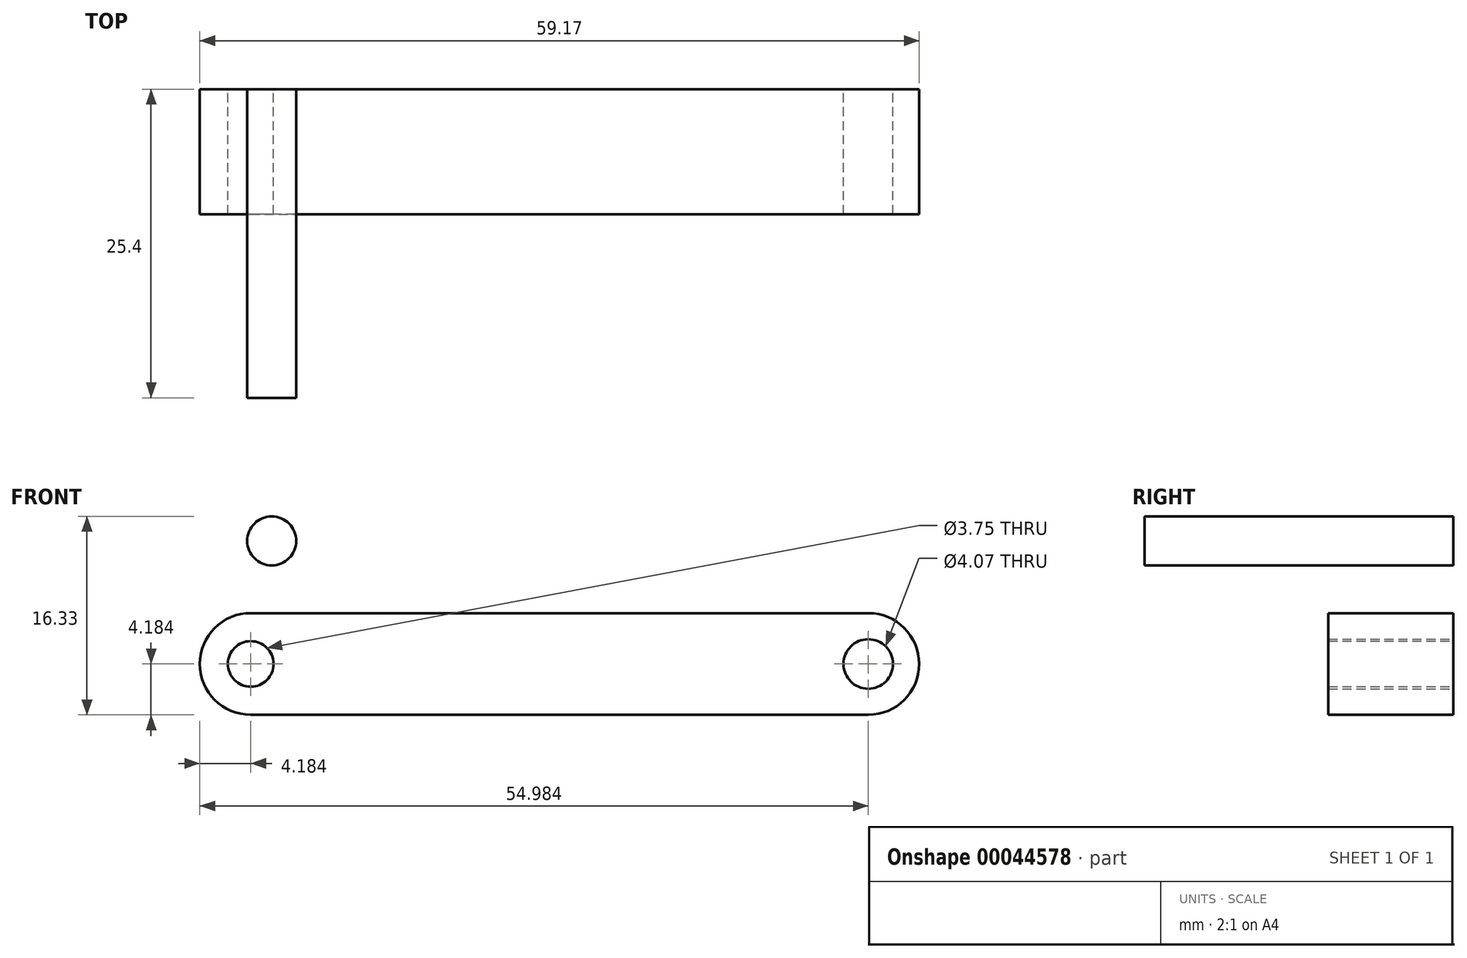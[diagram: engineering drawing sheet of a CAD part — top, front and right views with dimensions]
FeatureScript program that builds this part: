
annotation { "Feature Type Name" : "Feature", "Feature Type Description" : "" }
export const myFeature = defineFeature(function(context is Context, id is Id, definition is map)
    precondition{}
    {
        {
            var Q0;
            Q0=qCreatedBy(makeId("Front.planeOp"),FACE);
            var sketch = newSketch(context, id + "F0", { "sketchPlane" : qUnion([Q0])});
            skLineSegment(sketch, "E0", {"start": v(-62.77, 44.12) * mm, "end": v(-11.97, 44.12) * mm});
            skArc(sketch, "E1", {"start": v(-11.97, 35.75) * mm, "mid": v(-7.78, 39.93) * mm, "end": v(-11.97, 44.12) * mm});
            skLineSegment(sketch, "E2", {"start": v(-11.97, 35.75) * mm, "end": v(-62.77, 35.75) * mm});
            skArc(sketch, "E3", {"start": v(-62.77, 44.12) * mm, "mid": v(-66.95, 39.93) * mm, "end": v(-62.77, 35.75) * mm});
            skCircle(sketch, "E4", {"center": v(-62.77, 39.93) * mm, "radius": 1.88 * mm});
            skCircle(sketch, "E5", {"center": v(-11.97, 39.93) * mm, "radius": 2.04 * mm});
            skSolve(sketch);
        }
        {
            var Q0;
            Q0=makeQuery(id+"F0.imprint","IMPRINT",FACE,{"disambiguationData":[TD([[makeQuery(id+"F0.imprint","IMPRINT",EDGE,{"derivedFrom":sQuery(id+"F0.wireOp",EDGE,"E0")}),-1.0]])]});
            extrude(context, id + "F1", {"entities" : qUnion([Q0]), "depth" : 10.28 * mm});
        }
        {
            var Q0;
            Q0=qCreatedBy(makeId("Front.planeOp"),FACE);
            var sketch = newSketch(context, id + "F2", { "sketchPlane" : qUnion([Q0])});
            skCircle(sketch, "E6", {"center": v(-61.04, 50.06) * mm, "radius": 2.02 * mm});
            skSolve(sketch);
        }
        {
            var Q0;
            Q0=makeQuery(id+"F2.imprint","IMPRINT",FACE,{"disambiguationData":[TD([[makeQuery(id+"F2.imprint","IMPRINT",EDGE,{"derivedFrom":sQuery(id+"F2.wireOp",EDGE,"E6")}),1.0]])]});
            extrude(context, id + "F3", {"entities" : qUnion([Q0]), "depth" : 25.4 * mm});
        }
    });
